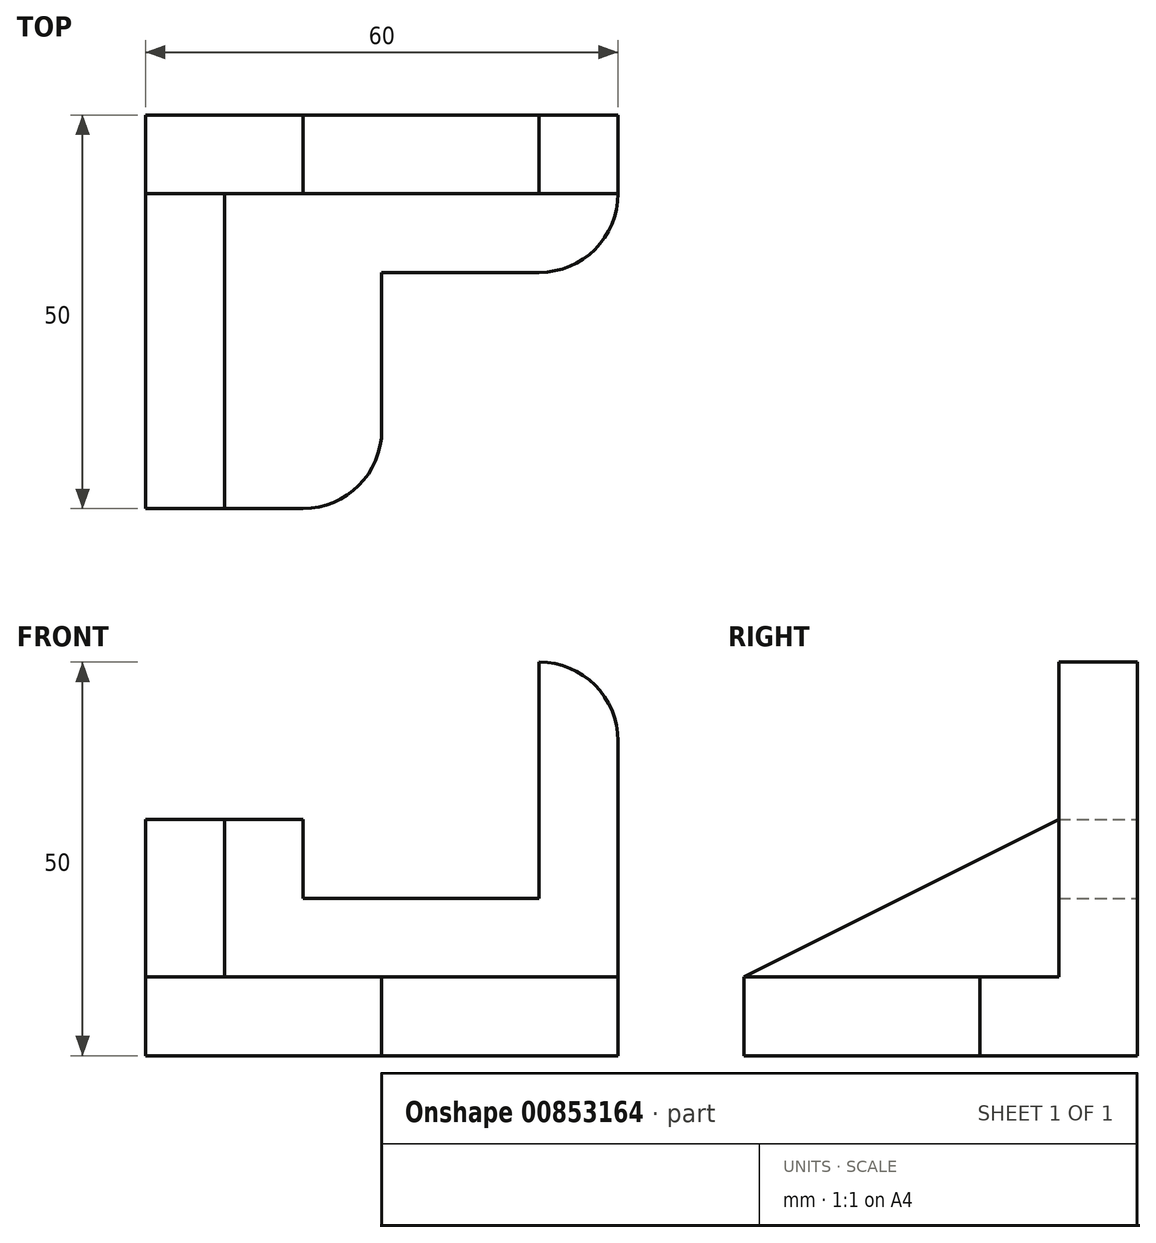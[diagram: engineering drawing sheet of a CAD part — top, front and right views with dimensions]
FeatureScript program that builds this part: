
annotation { "Feature Type Name" : "Feature", "Feature Type Description" : "" }
export const myFeature = defineFeature(function(context is Context, id is Id, definition is map)
    precondition{}
    {
        {
            var Q0;
            Q0=qCreatedBy(makeId("Top.planeOp"),FACE);
            var sketch = newSketch(context, id + "F0", { "sketchPlane" : qUnion([Q0])});
            skLineSegment(sketch, "E0", {"start": v(21.3, 40) * mm, "end": v(21.3, 50) * mm});
            skLineSegment(sketch, "E1", {"start": v(21.3, 50) * mm, "end": v(-38.7, 50) * mm});
            skLineSegment(sketch, "E2", {"start": v(-38.7, 50) * mm, "end": v(-38.7, 0) * mm});
            skLineSegment(sketch, "E3", {"start": v(-38.7, 0) * mm, "end": v(-18.7, 0) * mm});
            skLineSegment(sketch, "E4", {"start": v(-8.7, 10) * mm, "end": v(-8.7, 30) * mm});
            skLineSegment(sketch, "E5", {"start": v(-8.7, 30) * mm, "end": v(11.3, 30) * mm});
            skArc(sketch, "E6.filletArc", {"start": v(-18.7, 0) * mm, "mid": v(-11.64, 2.93) * mm, "end": v(-8.7, 10) * mm});
            skLineSegment(sketch, "E7", {"start": v(-38.7, 50) * mm, "end": v(-38.7, 40) * mm});
            skLineSegment(sketch, "E8", {"start": v(21.3, 40) * mm, "end": v(-38.7, 40) * mm});
            skLineSegment(sketch, "E9", {"start": v(21.3, 40) * mm, "end": v(21.3, 40) * mm});
            skLineSegment(sketch, "E10", {"start": v(11.3, 30) * mm, "end": v(11.3, 30) * mm});
            skArc(sketch, "E11.filletArc", {"start": v(11.3, 30) * mm, "mid": v(18.36, 32.93) * mm, "end": v(21.3, 40) * mm});
            skLineSegment(sketch, "E12", {"start": v(11.3, 40) * mm, "end": v(11.3, 50) * mm});
            skLineSegment(sketch, "E13", {"start": v(-38.7, 40) * mm, "end": v(-18.7, 40) * mm});
            skLineSegment(sketch, "E14", {"start": v(-18.7, 40) * mm, "end": v(-18.7, 50) * mm});
            skLineSegment(sketch, "E15", {"start": v(-38.7, 0) * mm, "end": v(-28.7, 0) * mm});
            skLineSegment(sketch, "E16", {"start": v(-28.7, 0) * mm, "end": v(-28.7, 40) * mm});
            skSolve(sketch);
        }
        {
            var Q0;
            Q0=makeQuery(id+"F0.imprint","IMPRINT",FACE,{"disambiguationData":[TD([[makeQuery(id+"F0.imprint","IMPRINT",EDGE,{"derivedFrom":sQuery(id+"F0.wireOp",EDGE,"E4")}),1.0]])]});
            extrude(context, id + "F1", {"entities" : qUnion([Q0]), "depth" : 10 * mm, "offsetDistance" : 25 * mm});
        }
        {
            var Q0;
            {var subQ0=sQuery(id+"F0.wireOp",EDGE,"E12");Q0=makeQuery(id+"F0.imprint","IMPRINT",FACE,{"disambiguationData":[TD([[makeQuery(id+"F0.imprint","IMPRINT",EDGE,{"derivedFrom":subQ0}),1.0]])]});}
            extrude(context, id + "F2", {"entities" : qUnion([Q0]), "operationType" : NewBodyOperationType.ADD, "depth" : 20 * mm, "offsetDistance" : 25 * mm});
        }
        {
            var Q0;
            {var subQ4=sQuery(id+"F0.wireOp",EDGE,"E14");Q0=makeQuery(id+"F0.imprint","IMPRINT",FACE,{"disambiguationData":[TD([[makeQuery(id+"F0.imprint","IMPRINT",EDGE,{"derivedFrom":subQ4}),1.0]])]});}
            extrude(context, id + "F3", {"entities" : qUnion([Q0]), "operationType" : NewBodyOperationType.ADD, "depth" : 30 * mm, "offsetDistance" : 25 * mm});
        }
        {
            var Q0;
            {var subQ0=sQuery(id+"F0.wireOp",EDGE,"E0");Q0=makeQuery(id+"F0.imprint","IMPRINT",FACE,{"disambiguationData":[TD([[makeQuery(id+"F0.imprint","IMPRINT",EDGE,{"derivedFrom":subQ0}),1.0]])]});}
            extrude(context, id + "F4", {"entities" : qUnion([Q0]), "operationType" : NewBodyOperationType.ADD, "depth" : 50 * mm, "offsetDistance" : 25 * mm});
        }
        {
            var Q0;
            {var subQ5=sQuery(id+"F0.wireOp",EDGE,"E16");Q0=makeQuery(id+"F0.imprint","IMPRINT",FACE,{"disambiguationData":[TD([[makeQuery(id+"F0.imprint","IMPRINT",EDGE,{"derivedFrom":subQ5}),1.0]])]});}
            extrude(context, id + "F5", {"entities" : qUnion([Q0]), "operationType" : NewBodyOperationType.ADD, "depth" : 30 * mm, "offsetDistance" : 25 * mm});
        }
        {
            var Q0;
            Q0=makeQuery(id+"F4.opExtrude","CAP_EDGE",EDGE,{"disambiguationData":[OSD([sQuery(id+"F0.wireOp",EDGE,"E0")])],"isStart":false});
            fillet(context, id + "F6", {"entities" : qUnion([Q0]), "radius" : 10 * mm, "tangentPropagation" : true, "allowEdgeOverflow" : false});
        }
        {
            var Q0;
            Q0=makeQuery(id+"F5.opExtrude","CAP_EDGE",EDGE,{"disambiguationData":[OSD([sQuery(id+"F0.wireOp",EDGE,"E3")])],"isStart":false});
            chamfer(context, id + "F7", {"entities" : qUnion([Q0]), "chamferType" : ChamferType.TWO_OFFSETS, "width1" : 40 * mm, "oppositeDirection" : false, "width2" : 20 * mm, "tangentPropagation" : true});
        }
    });
